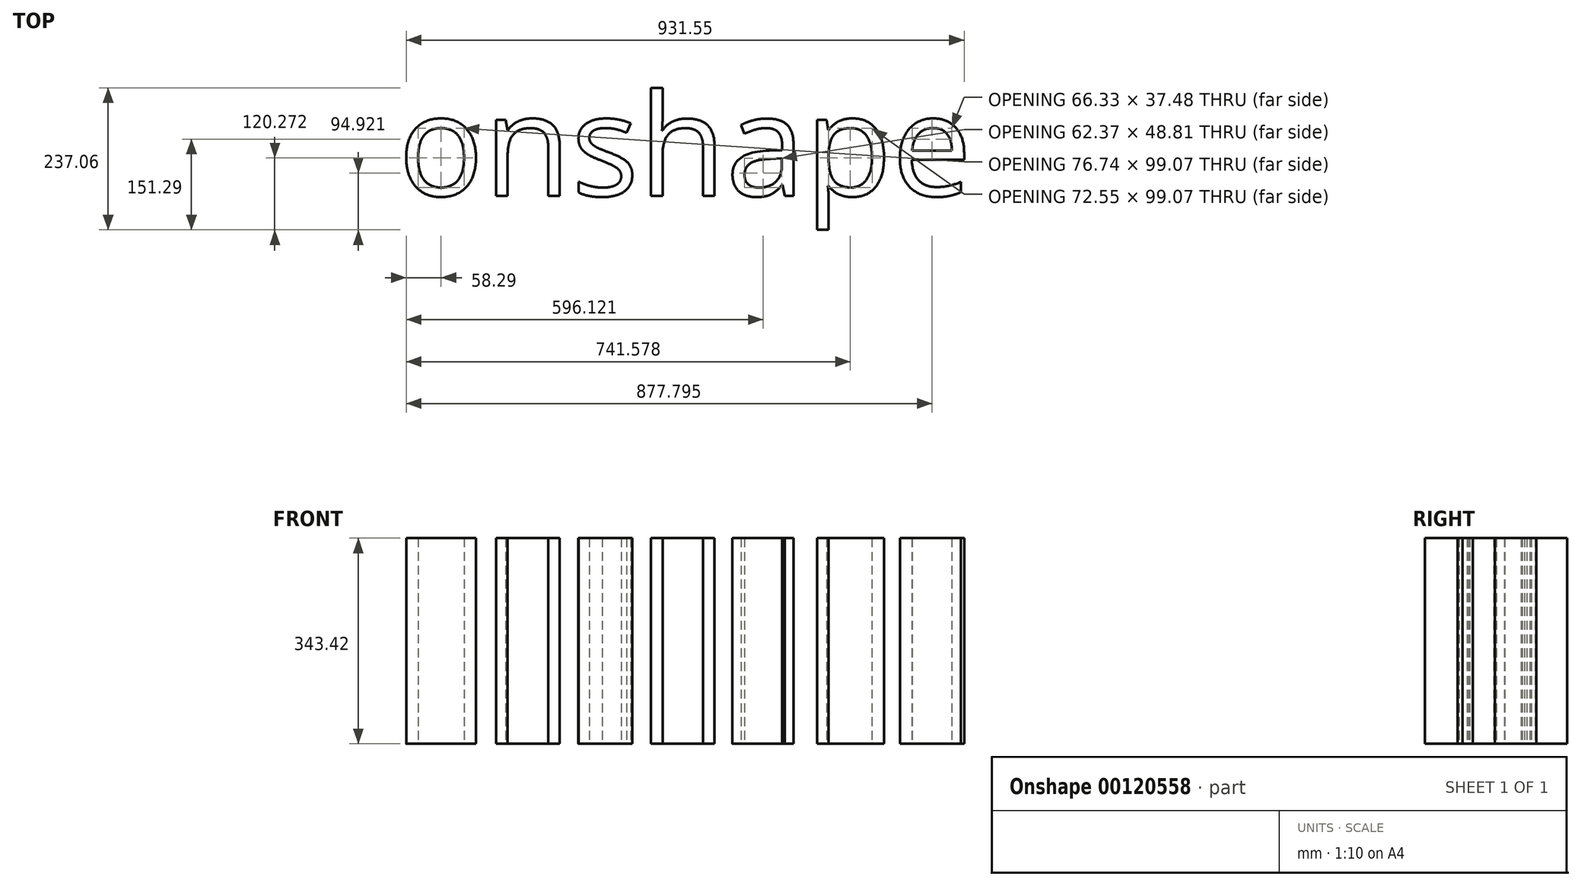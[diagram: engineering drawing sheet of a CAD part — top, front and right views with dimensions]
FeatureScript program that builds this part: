
annotation { "Feature Type Name" : "Feature", "Feature Type Description" : "" }
export const myFeature = defineFeature(function(context is Context, id is Id, definition is map)
    precondition{}
    {
        {
            var Q0;
            Q0=qCreatedBy(makeId("Top.planeOp"),FACE);
            var sketch = newSketch(context, id + "F2", { "sketchPlane" : qUnion([Q0])});
            skText(sketch, "E0", { "text": "onshape", "fontName": "OpenSans-Regular.ttf"});
            const initialGuessFNlLmd8FvFe8XWSbD_0  = {"E0": [0, 0, 1, 0, 0.17066]};
            skSetInitialGuess(sketch, initialGuessFNlLmd8FvFe8XWSbD_0);
            skSolve(sketch);
        }
        {
            var Q0;
            Q0=makeQuery(id+"F2.imprint","IMPRINT",FACE,{"disambiguationData":[TD([[makeQuery(id+"F2.imprint","IMPRINT",EDGE,{"derivedFrom":sQuery(id+"F2.wireOp",EDGE,"E0.sketch_text.stroke-0")}),-1.0]])]});
            extrude(context, id + "F0", {"entities" : qUnion([Q0]), "depth" : 25.4 * mm});
        }
        {
            var Q0;
            Q0 = qSketchRegion(id + "F2", true);
            extrude(context, id + "F1", {"entities" : qUnion([Q0]), "operationType" : NewBodyOperationType.ADD, "depth" : 343.42 * mm});
        }
    });
